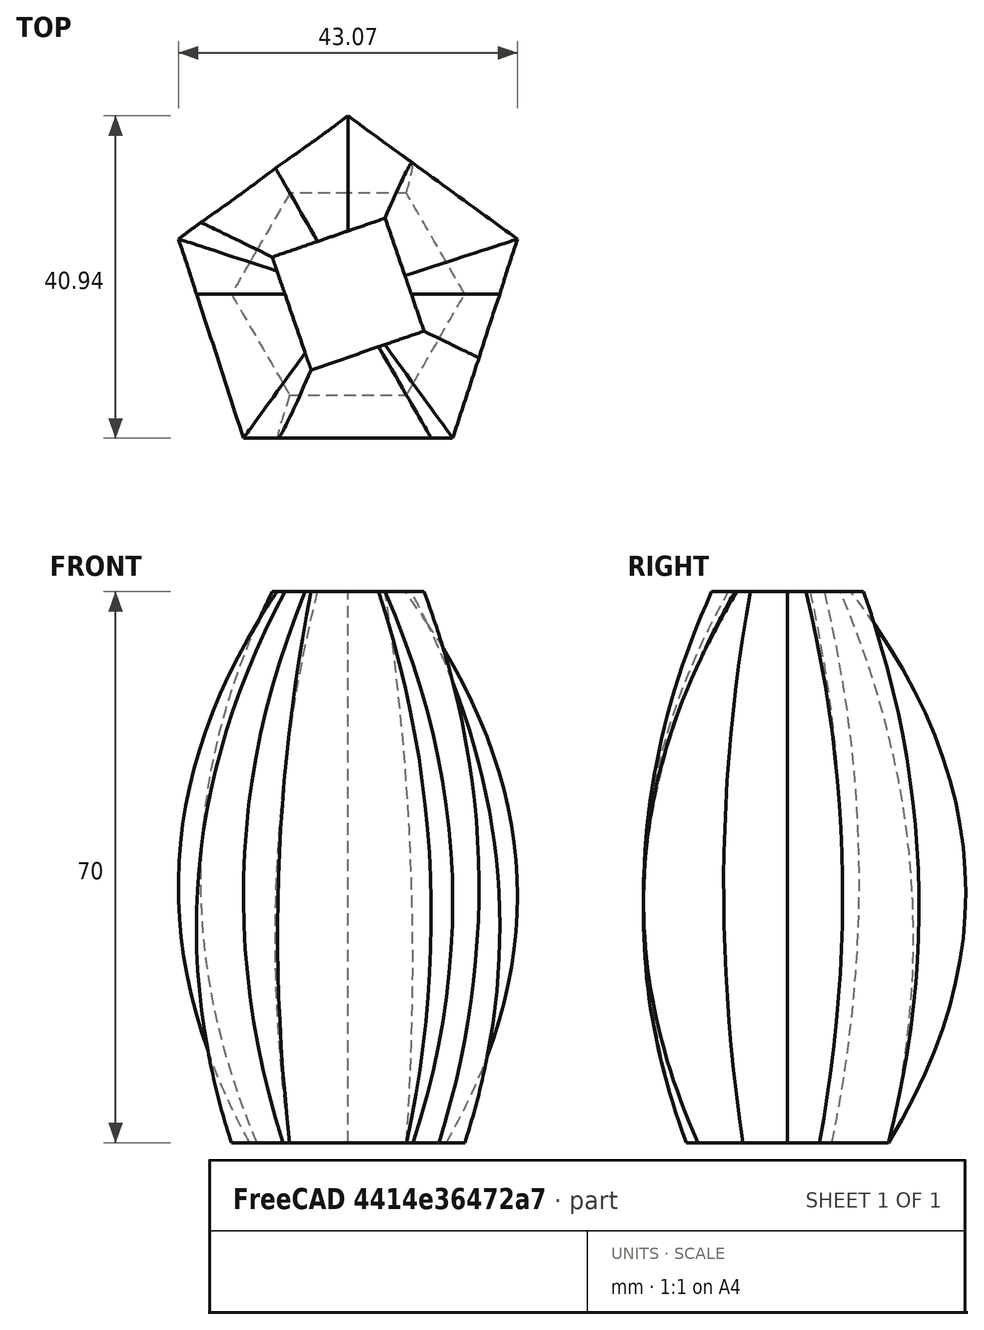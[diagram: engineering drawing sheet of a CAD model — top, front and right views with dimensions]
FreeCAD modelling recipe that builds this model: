
FCSTD DOCUMENT  (FreeCAD 1.0R38806 (Git))
Label: loft
License: All rights reserved
LicenseURL: http://en.wikipedia.org/wiki/All_rights_reserved
objects: Sketcher::SketchObject×3, PartDesign::Body×1, Part::Loft×1
note: 8 computed .brp shape members not serialized (recipe doc carries the construction recipe); baked Part::Feature solids carry a one-line shape summary decoded from their .brp

FEATURE [Sketcher::SketchObject] Sketch  label="1"
  ArcFitTolerance = 1e-06
  AttachmentSupport = -> [XY_Plane]
  FullyConstrained = false
  MakeInternals = false
  MapMode = 5
  sketch-geometry (7):
    g0: LineSegment StartX=7.41213 StartY=-12.8382 StartZ=0 EndX=14.8243 EndY=0 EndZ=0
    g1: LineSegment StartX=14.8243 StartY=0 StartZ=0 EndX=7.41213 EndY=12.8382 EndZ=0
    g2: LineSegment StartX=7.41213 StartY=12.8382 StartZ=0 EndX=-7.41213 EndY=12.8382 EndZ=0
    g3: LineSegment StartX=-7.41213 StartY=12.8382 StartZ=0 EndX=-14.8243 EndY=0 EndZ=0
    g4: LineSegment StartX=-14.8243 StartY=0 StartZ=0 EndX=-7.41213 EndY=-12.8382 EndZ=0
    g5: LineSegment StartX=-7.41213 StartY=-12.8382 StartZ=0 EndX=7.41213 EndY=-12.8382 EndZ=0
    g6: Circle [constr] CenterX=0 CenterY=0 CenterZ=0 NormalX=0 NormalY=0 NormalZ=1 AngleXU=0 Radius=14.8243
  constraints (15):
    c: Coincident(g0,g1)
    c: Coincident(g1,g2)
    c: Coincident(g2,g3)
    c: Coincident(g3,g4)
    c: Coincident(g4,g5)
    c: Coincident(g5,g0)
    c: Equal(g0, g1-g5) x5
    c: PointOnObject(g0,g6)
    c: PointOnObject(g1,g6)
    c: PointOnObject(g2,g6)
    c: PointOnObject(g3,g6)
    c: PointOnObject(g4,g6)
    c: PointOnObject(g5,g6)
    c: Coincident(g6,g-1)
    c: Horizontal(g5)
FEATURE [Sketcher::SketchObject] Sketch001  label="2"
  ArcFitTolerance = 1e-06
  AttachmentOffset = pos=(0,0,30) rot=(0,0,1;0rad)
  AttachmentSupport = -> [XY_Plane]
  FullyConstrained = false
  MakeInternals = false
  MapMode = 5
  Placement = pos=(0,0,30) rot=(0,0,1;0rad)
  sketch-geometry (6):
    g0: LineSegment StartX=13.2882 StartY=-18.2896 StartZ=0 EndX=21.5008 EndY=6.98602 EndZ=0
    g1: LineSegment StartX=21.5008 StartY=6.98602 StartZ=0 EndX=0 EndY=22.6072 EndZ=0
    g2: LineSegment StartX=0 StartY=22.6072 StartZ=0 EndX=-21.5008 EndY=6.98602 EndZ=0
    g3: LineSegment StartX=-21.5008 StartY=6.98602 StartZ=0 EndX=-13.2882 EndY=-18.2896 EndZ=0
    g4: LineSegment StartX=-13.2882 StartY=-18.2896 StartZ=0 EndX=13.2882 EndY=-18.2896 EndZ=0
    g5: Circle [constr] CenterX=0 CenterY=0 CenterZ=0 NormalX=0 NormalY=0 NormalZ=1 AngleXU=0 Radius=22.6072
  constraints (13):
    c: Coincident(g0,g1)
    c: Coincident(g1,g2)
    c: Coincident(g2,g3)
    c: Coincident(g3,g4)
    c: Coincident(g4,g0)
    c: Equal(g0, g1-g4) x4
    c: PointOnObject(g0,g5)
    c: PointOnObject(g1,g5)
    c: PointOnObject(g2,g5)
    c: PointOnObject(g3,g5)
    c: PointOnObject(g4,g5)
    c: Coincident(g5,g-1)
    c: PointOnObject(g1,g-2)
FEATURE [Sketcher::SketchObject] Sketch002  label="3"
  ArcFitTolerance = 1e-06
  AttachmentOffset = pos=(0,0,70) rot=(0,0,1;0.331613rad)
  AttachmentSupport = -> [XY_Plane]
  FullyConstrained = false
  MakeInternals = false
  MapMode = 5
  Placement = pos=(0,0,70) rot=(0,0,1;0.331613rad)
  sketch-geometry (5):
    g0: LineSegment StartX=7.58548 StartY=-7.58548 StartZ=0 EndX=7.58548 EndY=7.58548 EndZ=0
    g1: LineSegment StartX=7.58548 StartY=7.58548 StartZ=0 EndX=-7.58548 EndY=7.58548 EndZ=0
    g2: LineSegment StartX=-7.58548 StartY=7.58548 StartZ=0 EndX=-7.58548 EndY=-7.58548 EndZ=0
    g3: LineSegment StartX=-7.58548 StartY=-7.58548 StartZ=0 EndX=7.58548 EndY=-7.58548 EndZ=0
    g4: Circle [constr] CenterX=0 CenterY=0 CenterZ=0 NormalX=0 NormalY=0 NormalZ=1 AngleXU=0 Radius=10.7275
  constraints (13):
    c: Coincident(g0,g1)
    c: Coincident(g1,g2)
    c: Coincident(g2,g3)
    c: Coincident(g3,g0)
    c: Equal(g0,g1)
    c: Equal(g0,g2)
    c: Equal(g0,g3)
    c: PointOnObject(g0,g4)
    c: PointOnObject(g1,g4)
    c: PointOnObject(g2,g4)
    c: PointOnObject(g3,g4)
    c: Coincident(g4,g-1)
    c: Horizontal(g3)
FEATURE [PartDesign::Body] Body
  AllowCompound = false
  Group = -> [Sketch,Sketch001,Sketch002]
  Origin = -> Origin
FEATURE [Part::Loft] Loft
  Closed = false
  MaxDegree = 5
  Ruled = false
  Sections = -> [Sketch,Sketch001,Sketch002]
  Solid = true
